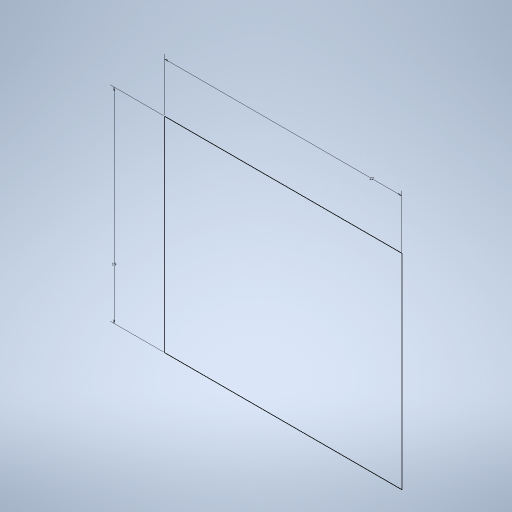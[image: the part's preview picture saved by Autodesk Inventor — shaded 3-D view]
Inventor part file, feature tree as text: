
AUTODESK INVENTOR PART (.ipt)
format: ipt  version: 2023 (Build 270158000, 158)  size: 232,448 bytes
history: native  units: in
note: dims shown in document units (in); Inventor stores cm internally (conversion verified against a paired STEP export)
features: sketch x1
ambient origin geometry x8: Origin, YZ Plane, XZ Plane, XY Plane, X Axis, Y Axis, Z Axis, Center Point
feature tree (1):
  sketch  "Sketch1"  dims[d0=0.8661in d1=0.748in]
